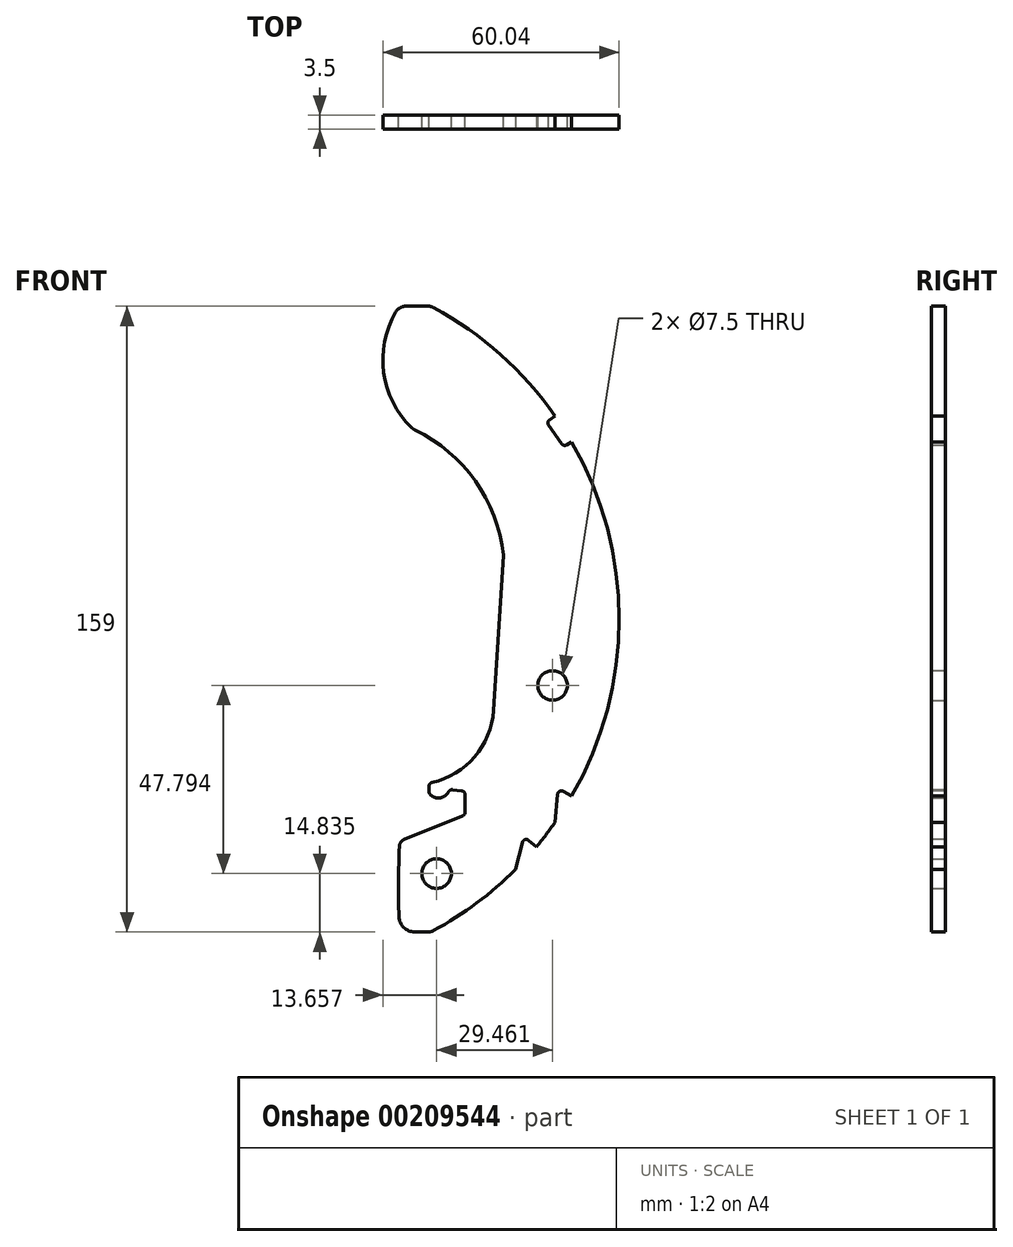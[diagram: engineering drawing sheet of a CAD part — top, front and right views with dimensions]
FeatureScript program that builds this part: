
annotation { "Feature Type Name" : "Feature", "Feature Type Description" : "" }
export const myFeature = defineFeature(function(context is Context, id is Id, definition is map)
    precondition{}
    {
        {
            var Q0;
            Q0=qCreatedBy(makeId("Front.planeOp"),FACE);
            var sketch = newSketch(context, id + "F0", { "sketchPlane" : qUnion([Q0])});
            skArc(sketch, "E0", {"start": v(42.86, -79.14) * mm, "mid": v(90, 0) * mm, "end": v(42.86, 79.14) * mm});
            skLineSegment(sketch, "E1", {"start": v(42.19, 79.5) * mm, "end": v(42.19, -79.5) * mm, "construction": true});
            skLineSegment(sketch, "E2", {"start": v(42.19, 0) * mm, "end": v(0, 0) * mm, "construction": true});
            skLineSegment(sketch, "E3", {"start": v(0, 0) * mm, "end": v(43.62, -64.66) * mm, "construction": true});
            skLineSegment(sketch, "E4", {"start": v(0, 0) * mm, "end": v(38.1, -22) * mm, "construction": true});
            skLineSegment(sketch, "E5", {"start": v(0, 0) * mm, "end": v(73.08, -16.87) * mm, "construction": true});
            skLineSegment(sketch, "E6", {"start": v(0, 0) * mm, "end": v(20.78, 12) * mm, "construction": true});
            skPoint(sketch, "E7", {"position": v(43.62, -64.66) * mm});
            skPoint(sketch, "E8", {"position": v(73.08, -16.87) * mm});
            skArc(sketch, "E9", {"start": v(27.75, -4.9) * mm, "mid": v(26.9, -5.44) * mm, "end": v(26.08, -6.02) * mm});
            skArc(sketch, "E10", {"start": v(18.85, -27.95) * mm, "mid": v(18.93, -27.96) * mm, "end": v(19.01, -27.96) * mm, "construction": true});
            skLineSegment(sketch, "E11", {"start": v(0, 0) * mm, "end": v(37.7, 48.25) * mm, "construction": true});
            skLineSegment(sketch, "E12", {"start": v(0, 0) * mm, "end": v(60.56, 16.23) * mm, "construction": true});
            skArc(sketch, "E13.trimOffspring", {"start": v(60.55, 16.31) * mm, "mid": v(53.45, 35.1) * mm, "end": v(38.1, 48.05) * mm});
            skLineSegment(sketch, "E14", {"start": v(0, 0) * mm, "end": v(53.7, -9.47) * mm, "construction": true});
            skLineSegment(sketch, "E15", {"start": v(0, 0) * mm, "end": v(41.68, -41.68) * mm, "construction": true});
            skArc(sketch, "E16.trimOffspring", {"start": v(19.01, -27.96) * mm, "mid": v(19.08, -28.18) * mm, "end": v(19.16, -28.4) * mm, "construction": true});
            skArc(sketch, "E17.trimOffspring", {"start": v(42.46, -41.52) * mm, "mid": v(53.3, -35) * mm, "end": v(58.07, -23.26) * mm});
            skLineSegment(sketch, "E18", {"start": v(60.56, 16.14) * mm, "end": v(58.07, -23.26) * mm});
            skLineSegment(sketch, "E19", {"start": v(41.43, -79.5) * mm, "end": v(38.06, -79.5) * mm});
            skPoint(sketch, "E20", {"position": v(34.19, -56.5) * mm});
            skArc(sketch, "E21", {"start": v(34.14, -57.8) * mm, "mid": v(33.96, -66.7) * mm, "end": v(34.06, -75.6) * mm});
            skLineSegment(sketch, "E22", {"start": v(35.39, -56.01) * mm, "end": v(50.25, -50) * mm});
            skLineSegment(sketch, "E23", {"start": v(50.87, -49.07) * mm, "end": v(50.87, -44.63) * mm});
            skLineSegment(sketch, "E24", {"start": v(50, -43.64) * mm, "end": v(47.68, -43.35) * mm});
            skLineSegment(sketch, "E25", {"start": v(41.68, -42.5) * mm, "end": v(41.68, -43.84) * mm});
            skArc(sketch, "E26", {"start": v(41.94, -44.5) * mm, "mid": v(44.47, -45.44) * mm, "end": v(46.67, -43.89) * mm});
            skPoint(sketch, "E27.visualSharp", {"position": v(50.87, -49.75) * mm});
            skArc(sketch, "E27.filletArc", {"start": v(50.25, -50) * mm, "mid": v(50.7, -49.63) * mm, "end": v(50.87, -49.07) * mm});
            skPoint(sketch, "E28.visualSharp", {"position": v(50.87, -43.75) * mm});
            skArc(sketch, "E28.filletArc", {"start": v(50.87, -44.63) * mm, "mid": v(50.62, -43.97) * mm, "end": v(50, -43.64) * mm});
            skArc(sketch, "E29.filletArc", {"start": v(35.39, -56.01) * mm, "mid": v(34.5, -56.72) * mm, "end": v(34.14, -57.8) * mm});
            skPoint(sketch, "E30.visualSharp", {"position": v(34.19, -79.5) * mm});
            skArc(sketch, "E30.filletArc", {"start": v(34.06, -75.6) * mm, "mid": v(35.27, -78.36) * mm, "end": v(38.06, -79.5) * mm});
            skPoint(sketch, "E31.visualSharp", {"position": v(42.19, -79.5) * mm});
            skArc(sketch, "E31.filletArc", {"start": v(41.43, -79.5) * mm, "mid": v(42.17, -79.4) * mm, "end": v(42.86, -79.14) * mm});
            skPoint(sketch, "E32.visualSharp", {"position": v(41.68, -44.18) * mm});
            skArc(sketch, "E32.filletArc", {"start": v(41.68, -43.84) * mm, "mid": v(41.75, -44.2) * mm, "end": v(41.94, -44.5) * mm});
            skPoint(sketch, "E33.visualSharp", {"position": v(41.68, -41.68) * mm});
            skArc(sketch, "E33.filletArc", {"start": v(42.46, -41.52) * mm, "mid": v(41.9, -41.87) * mm, "end": v(41.68, -42.5) * mm});
            skPoint(sketch, "E34.visualSharp", {"position": v(46.9, -43.25) * mm});
            skArc(sketch, "E34.filletArc", {"start": v(47.68, -43.35) * mm, "mid": v(47.09, -43.46) * mm, "end": v(46.67, -43.89) * mm});
            skPoint(sketch, "E35.visualSharp", {"position": v(60.56, 16.23) * mm});
            skArc(sketch, "E35.filletArc", {"start": v(60.56, 16.14) * mm, "mid": v(60.56, 16.23) * mm, "end": v(60.55, 16.31) * mm});
            skLineSegment(sketch, "E36", {"start": v(41.43, 79.5) * mm, "end": v(35.83, 79.5) * mm});
            skArc(sketch, "E37", {"start": v(33.24, 78.01) * mm, "mid": v(30.19, 62.6) * mm, "end": v(37.33, 48.6) * mm});
            skPoint(sketch, "E38.visualSharp", {"position": v(34.19, 79.5) * mm});
            skArc(sketch, "E38.filletArc", {"start": v(35.83, 79.5) * mm, "mid": v(34.34, 79.1) * mm, "end": v(33.24, 78.01) * mm});
            skPoint(sketch, "E39.visualSharp", {"position": v(42.19, 79.5) * mm});
            skArc(sketch, "E39.filletArc", {"start": v(42.86, 79.14) * mm, "mid": v(42.17, 79.4) * mm, "end": v(41.43, 79.5) * mm});
            skPoint(sketch, "E40.visualSharp", {"position": v(37.7, 48.25) * mm});
            skArc(sketch, "E40.filletArc", {"start": v(37.33, 48.6) * mm, "mid": v(37.7, 48.3) * mm, "end": v(38.1, 48.05) * mm});
            skSolve(sketch);
        }
        {
            var Q0;
            Q0=makeQuery(id+"F0.imprint","IMPRINT",FACE,{"disambiguationData":[TD([[makeQuery(id+"F0.imprint","IMPRINT",EDGE,{"derivedFrom":sQuery(id+"F0.wireOp",EDGE,"E0")}),1.0]])]});
            extrude(context, id + "F1", {"entities" : qUnion([Q0]), "depth" : 3.5 * mm});
        }
        {
            var Q0;
            Q0=sQuery(id+"F0.wireOp",VERTEX,"E8");
            var Q1;
            Q1=sQuery(id+"F0.wireOp",VERTEX,"E7");
            var Q2;
            Q2=makeQuery(id+"F1.opExtrude","SWEPT_BODY",BODY,{"disambiguationData":[OSD([sQuery(id+"F0.wireOp",EDGE,"E0"),sQuery(id+"F0.wireOp",EDGE,"E13.trimOffspring"),sQuery(id+"F0.wireOp",EDGE,"E17.trimOffspring"),sQuery(id+"F0.wireOp",EDGE,"E18"),sQuery(id+"F0.wireOp",EDGE,"E19"),sQuery(id+"F0.wireOp",EDGE,"E21"),sQuery(id+"F0.wireOp",EDGE,"E22"),sQuery(id+"F0.wireOp",EDGE,"E23"),sQuery(id+"F0.wireOp",EDGE,"E24"),sQuery(id+"F0.wireOp",EDGE,"E25"),sQuery(id+"F0.wireOp",EDGE,"E26"),sQuery(id+"F0.wireOp",EDGE,"E27.filletArc"),sQuery(id+"F0.wireOp",EDGE,"E28.filletArc"),sQuery(id+"F0.wireOp",EDGE,"E29.filletArc"),sQuery(id+"F0.wireOp",EDGE,"E30.filletArc"),sQuery(id+"F0.wireOp",EDGE,"E31.filletArc"),sQuery(id+"F0.wireOp",EDGE,"E32.filletArc"),sQuery(id+"F0.wireOp",EDGE,"E33.filletArc"),sQuery(id+"F0.wireOp",EDGE,"E34.filletArc"),sQuery(id+"F0.wireOp",EDGE,"E35.filletArc"),sQuery(id+"F0.wireOp",EDGE,"E36"),sQuery(id+"F0.wireOp",EDGE,"E37"),sQuery(id+"F0.wireOp",EDGE,"E38.filletArc"),sQuery(id+"F0.wireOp",EDGE,"E39.filletArc"),sQuery(id+"F0.wireOp",EDGE,"E40.filletArc")])]});
            hole(context, id + "F2", {"style" : HoleStyle.SIMPLE, "endStyle" : HoleEndStyle.THROUGH, "oppositeDirection" : true, "holeDiameter" : 7.5 * mm, "locations" : qUnion([Q0, Q1]), "scope" : qUnion([Q2]), "isTappedThrough" : true});
        }
        {
            var Q0;
            Q0=makeQuery(id+"F1.opExtrude","CAP_FACE",FACE,{"disambiguationData":[OSD([sQuery(id+"F0.wireOp",EDGE,"E0"),sQuery(id+"F0.wireOp",EDGE,"E13.trimOffspring"),sQuery(id+"F0.wireOp",EDGE,"E17.trimOffspring"),sQuery(id+"F0.wireOp",EDGE,"E18"),sQuery(id+"F0.wireOp",EDGE,"E19"),sQuery(id+"F0.wireOp",EDGE,"E21"),sQuery(id+"F0.wireOp",EDGE,"E22"),sQuery(id+"F0.wireOp",EDGE,"E23"),sQuery(id+"F0.wireOp",EDGE,"E24"),sQuery(id+"F0.wireOp",EDGE,"E25"),sQuery(id+"F0.wireOp",EDGE,"E26"),sQuery(id+"F0.wireOp",EDGE,"E27.filletArc"),sQuery(id+"F0.wireOp",EDGE,"E28.filletArc"),sQuery(id+"F0.wireOp",EDGE,"E29.filletArc"),sQuery(id+"F0.wireOp",EDGE,"E30.filletArc"),sQuery(id+"F0.wireOp",EDGE,"E31.filletArc"),sQuery(id+"F0.wireOp",EDGE,"E32.filletArc"),sQuery(id+"F0.wireOp",EDGE,"E33.filletArc"),sQuery(id+"F0.wireOp",EDGE,"E34.filletArc"),sQuery(id+"F0.wireOp",EDGE,"E35.filletArc"),sQuery(id+"F0.wireOp",EDGE,"E36"),sQuery(id+"F0.wireOp",EDGE,"E37"),sQuery(id+"F0.wireOp",EDGE,"E38.filletArc"),sQuery(id+"F0.wireOp",EDGE,"E39.filletArc"),sQuery(id+"F0.wireOp",EDGE,"E40.filletArc")])],"isStart":false});
            var sketch = newSketch(context, id + "F3", { "sketchPlane" : qUnion([Q0])});
            skArc(sketch, "E41.0", {"start": v(42.86, -79.14) * mm, "mid": v(90, 0) * mm, "end": v(42.86, 79.14) * mm});
            skLineSegment(sketch, "E42", {"start": v(0, 0) * mm, "end": v(68.94, -57.85) * mm, "construction": true});
            skLineSegment(sketch, "E43", {"start": v(0, 0) * mm, "end": v(73.72, -51.62) * mm, "construction": true});
            skLineSegment(sketch, "E44", {"start": v(0, 0) * mm, "end": v(77.94, -45) * mm, "construction": true});
            skLineSegment(sketch, "E45", {"start": v(0, 0) * mm, "end": v(77.94, 45) * mm, "construction": true});
            skLineSegment(sketch, "E46", {"start": v(0, 0) * mm, "end": v(73.72, 51.62) * mm, "construction": true});
            skLineSegment(sketch, "E47", {"start": v(0, 0) * mm, "end": v(63.64, -63.64) * mm, "construction": true});
            skLineSegment(sketch, "E48", {"start": v(73.72, 51.62) * mm, "end": v(72.3, 50.63) * mm});
            skLineSegment(sketch, "E49", {"start": v(72.06, 49.24) * mm, "end": v(75.34, 44.55) * mm});
            skLineSegment(sketch, "E50", {"start": v(76.66, 44.26) * mm, "end": v(77.94, 45) * mm});
            skLineSegment(sketch, "E51", {"start": v(63.64, -63.64) * mm, "end": v(65.4, -56.75) * mm});
            skLineSegment(sketch, "E52", {"start": v(67.01, -56.23) * mm, "end": v(68.94, -57.85) * mm});
            skLineSegment(sketch, "E53", {"start": v(73.72, -51.62) * mm, "end": v(74.34, -44.56) * mm});
            skLineSegment(sketch, "E54", {"start": v(75.84, -43.79) * mm, "end": v(77.94, -45) * mm});
            skPoint(sketch, "E55.visualSharp", {"position": v(65.8, -55.2) * mm});
            skArc(sketch, "E55.filletArc", {"start": v(67.01, -56.23) * mm, "mid": v(66.06, -56.05) * mm, "end": v(65.4, -56.75) * mm});
            skPoint(sketch, "E56.visualSharp", {"position": v(74.48, -43) * mm});
            skArc(sketch, "E56.filletArc", {"start": v(75.84, -43.79) * mm, "mid": v(74.88, -43.77) * mm, "end": v(74.34, -44.56) * mm});
            skPoint(sketch, "E57.visualSharp", {"position": v(71.49, 50.06) * mm});
            skArc(sketch, "E57.filletArc", {"start": v(72.3, 50.63) * mm, "mid": v(71.9, 49.98) * mm, "end": v(72.06, 49.24) * mm});
            skPoint(sketch, "E58.visualSharp", {"position": v(75.87, 43.8) * mm});
            skArc(sketch, "E58.filletArc", {"start": v(75.34, 44.55) * mm, "mid": v(75.94, 44.15) * mm, "end": v(76.66, 44.26) * mm});
            skSolve(sketch);
        }
        {
            var Q0;
            {var subQ1=sQuery(id+"F3.wireOp",EDGE,"E48");Q0=makeQuery(id+"F3.imprint","IMPRINT",FACE,{"disambiguationData":[TD([[makeQuery(id+"F3.imprint","IMPRINT",EDGE,{"derivedFrom":subQ1}),1.0]])]});}
            var Q1;
            {var subQ0=sQuery(id+"F3.wireOp",EDGE,"E53");Q1=makeQuery(id+"F3.imprint","IMPRINT",FACE,{"disambiguationData":[TD([[makeQuery(id+"F3.imprint","IMPRINT",EDGE,{"derivedFrom":subQ0}),-1.0]])]});}
            var Q2;
            {var subQ0=sQuery(id+"F3.wireOp",EDGE,"E51");Q2=makeQuery(id+"F3.imprint","IMPRINT",FACE,{"disambiguationData":[TD([[makeQuery(id+"F3.imprint","IMPRINT",EDGE,{"derivedFrom":subQ0}),-1.0]])]});}
            extrude(context, id + "F4", {"entities" : qUnion([Q0, Q1, Q2]), "operationType" : NewBodyOperationType.REMOVE, "oppositeDirection" : true, "depth" : 25 * mm});
        }
    });
